# Revit family: LEGRAND_ECLAIRAGE_DE_SECURITE_SOURCE_CENTRALE
name_source: partatom
category: Luminaires
units: mm (PartAtom-declared; Revit-internal decimal feet)

## family parameters
Cote de connecteur circulaire = Utiliser le diamètre
Couper avec des vides une fois chargée = Non
Hôte = Face
Partagée = Non
Point de calcul de pièce = Non
Source d'éclairage = Non
Type d'élément = Normal

## types (8) — shared parameters
Accessoire non disponible = Pas d'accessoire ou Non disponible
Adapté au style de marquage = autre
Alimentation = central (batterie centrale)
Classe de protection = II
Condition Générale d'Utilisation = https://export.legrand.com
Couleur du boitier = blanc
Elévation par défaut = 1219 mm
Etat des accus = non applicable
Fabricant = LEGRAND
Forme alternative = IP_43-66 : IP_43
Installation de surveillance = sans
Largeur = 125 mm  [stored 0.410105 ft]
Longueur = 225 mm  [stored 0.738189 ft]
Matériau du boitier = LEGRAND - Plastique
Objet connecté = Non
Porte_picto = Porte picto Triangulaire Ref 062676
Source lumineuse = LED non interchangeable
Température utilisation (Min-Max °C) = -5-35
Type de borne = borne automatique
Type de commutation = circuit permanent-circuit de secours
Type de montage = montage en saillie-encastrement
URL = http://www.legrandoc.com
zero-valued in all types: Autonomie (H), Diamètre externe, Largeur de montage, Longeur d'encastrement, Profondeur d'encastrement

## per-type parameters (varying)
| type | Accessoire 1 | Accessoire 2 | Accessoire 3 | Accessoire 4 | Classe de protection (IP) | Consommation veille (mA) | Description | Entre axe fixation horizontale (Min-Max) (mm) | Entre axe fixation verticale (Min-Max) (mm) | Flux lumineux en mode d'urgence (lm) | Form | Fréquence (Hz) | Hauteur-Profondeur | IP 66 | Modèle | Picto | Puissance de la lampe (W) | Resistance aux chocs IK | Tension nominale (Min-Max V) | Type de tension |
| Amb_IP43_24V | Encastrement sans plaque Ref 062694 | Suspension BAES et LSC Ref 062677 | Pas d'accessoire ou Non disponible | Pas d'accessoire ou Non disponible | IP43 | 5 | LSC AMBIANCE A LEDS PLASTIQUE IP43 IK07 24 V DC | 60-162 | 0-90 | 400 | IP_43-66 : IP_43 |  | 45 mm  [stored 0.147638 ft] | Non | 062845 | Pas de picto | 4.1 | IK07 | 20.4-28 | CC |
| Amb_IP43_48-230V | Encastrement sans plaque Ref 062694 | Suspension BAES et LSC Ref 062677 | Pas d'accessoire ou Non disponible | Pas d'accessoire ou Non disponible | IP43 | 115 | LSC AMBIANCE A LEDS PLASTIQUE IP43 IK07 48 V DC A 230 V AC | 60-162 | 0-90 | 400 | IP_43-66 : IP_43 | 0-60 | 45 mm  [stored 0.147638 ft] | Non | 062945 | Pas de picto | 5.5 | IK07 | 40.2-253 | CA-CC |
| Evac_IP43_24V | Encastrement sans plaque Ref 062694 | Porte picto Vertical Ref 062675 | Suspension avec plaque BAES et LSC Ref 062677+062675 | Suspension BAES et LSC Ref 062677 | IP43 | 62 | LSC EVACUATION A LEDS PLASTIQUE IP43 IK07 24 V DC | 60-162 | 0-90 | 45 | IP_43-66 : IP_43 |  | 45 mm  [stored 0.147638 ft] | Non | 062815 | Picto Evac | 1.5 | IK07 | 20.4-28 | CC |
| Evac_IP43_48-230V | Encastrement sans plaque Ref 062694 | Porte picto Vertical Ref 062675 | Suspension avec plaque BAES et LSC Ref 062677+062675 | Suspension BAES et LSC Ref 062677 | IP43 | 19 | LSC EVACUATION A LEDS PLASTIQUE IP43 IK 07 48 V DC A 230 V AC | 60-162 | 0-90 | 45 | IP_43-66 : IP_43 | 0-60 | 45 mm  [stored 0.147638 ft] | Non | 062915 | Picto Evac | 1.1 | IK07 | 40.2-253 | CA-CC |
| Amb_IP66_24V | Pas d'accessoire ou Non disponible | Pas d'accessoire ou Non disponible | Pas d'accessoire ou Non disponible | Pas d'accessoire ou Non disponible | IP66 | 5 | LSC AMBIANCE A LEDS PLASTIQUE IP66 IK10 24 V DC | 80-150 | 0-80 | 400 | IP_43-66 : IP_66 |  | 62 mm  [stored 0.203412 ft] | Oui | 062846 | Pas de picto | 4.1 | IK10 | 20.4-28 | CC |
| Amb_IP66_48-230V | Pas d'accessoire ou Non disponible | Pas d'accessoire ou Non disponible | Pas d'accessoire ou Non disponible | Pas d'accessoire ou Non disponible | IP66 | 115 | LSC AMBIANCE A LEDS PLASTIQUE IP66 IK10 48 V DC A 230 V AC | 80-150 | 0-80 | 400 | IP_43-66 : IP_66 | 0-60 | 62 mm  [stored 0.203412 ft] | Oui | 062946 | Pas de picto | 5.5 | IK10 | 40.2-253 | CA-CC |
| Evac_IP66_24V | Porte picto Triangulaire Ref 062676 | Pas d'accessoire ou Non disponible | Pas d'accessoire ou Non disponible | Pas d'accessoire ou Non disponible | IP66 | 62 | LSC EVACUATION A LEDS PLASTIQUE IP66 IK10 24 V DC | 80-150 | 0-80 | 45 | IP_43-66 : IP_66 |  | 62 mm  [stored 0.203412 ft] | Oui | 062816 | Picto Evac | 1.5 | IK10 | 20.4-28 | CC |
| Evac_IP66_48-230V | Porte picto Triangulaire Ref 062676 | Pas d'accessoire ou Non disponible | Pas d'accessoire ou Non disponible | Pas d'accessoire ou Non disponible | IP66 | 19 | LSC EVACUATION A LEDS PLASTIQUE IP66 IK10 48 V DC A 230 V AC | 80-150 | 0-80 | 45 | IP_43-66 : IP_66 | 0-60 | 62 mm  [stored 0.203412 ft] | Oui | 062916 | Picto Evac | 1.1 | IK10 | 40.2-253 | CA-CC |

note: [stored X ft] marks values corroborated as IEEE doubles in the binary element streams (Revit-internal decimal feet)
